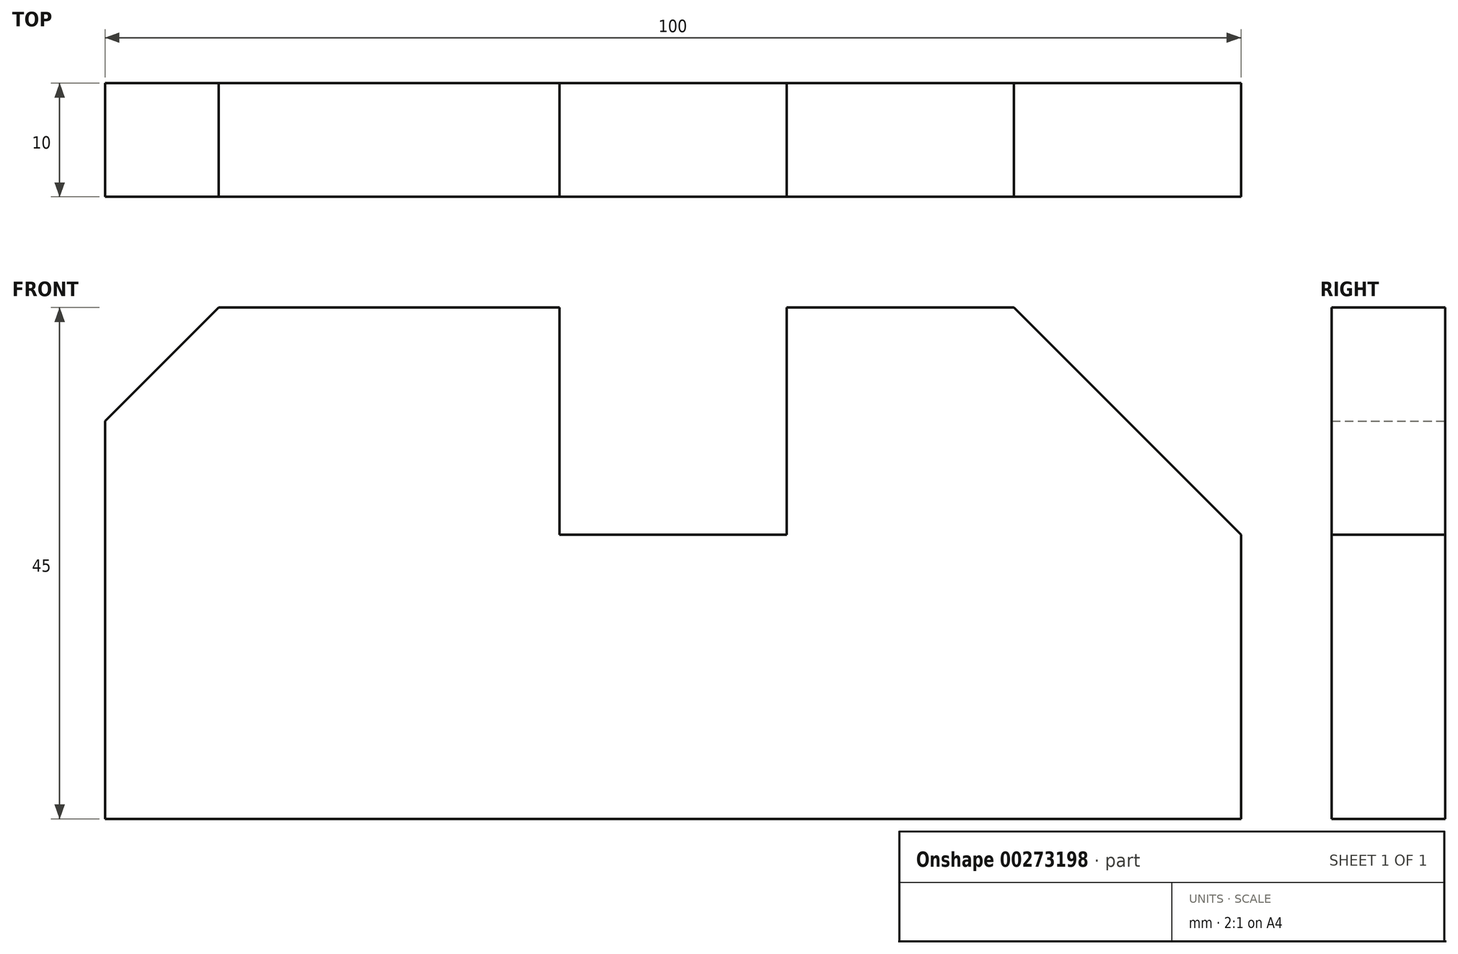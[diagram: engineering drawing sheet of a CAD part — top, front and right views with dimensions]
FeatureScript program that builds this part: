
annotation { "Feature Type Name" : "Feature", "Feature Type Description" : "" }
export const myFeature = defineFeature(function(context is Context, id is Id, definition is map)
    precondition{}
    {
        {
            var Q0;
            Q0=qCreatedBy(makeId("Front.planeOp"),FACE);
            var sketch = newSketch(context, id + "F0", { "sketchPlane" : qUnion([Q0])});
            skLineSegment(sketch, "E0", {"start": v(0, 0) * mm, "end": v(0, 35) * mm});
            skLineSegment(sketch, "E1", {"start": v(0, 35) * mm, "end": v(10, 45) * mm});
            skLineSegment(sketch, "E2", {"start": v(10, 45) * mm, "end": v(40, 45) * mm});
            skLineSegment(sketch, "E3", {"start": v(40, 45) * mm, "end": v(40, 25) * mm});
            skLineSegment(sketch, "E4", {"start": v(40, 25) * mm, "end": v(60, 25) * mm});
            skLineSegment(sketch, "E5", {"start": v(60, 25) * mm, "end": v(60, 45) * mm});
            skLineSegment(sketch, "E6", {"start": v(60, 45) * mm, "end": v(80, 45) * mm});
            skLineSegment(sketch, "E7", {"start": v(80, 45) * mm, "end": v(100, 25) * mm});
            skLineSegment(sketch, "E8", {"start": v(100, 25) * mm, "end": v(100, 0) * mm});
            skLineSegment(sketch, "E9", {"start": v(100, 0) * mm, "end": v(0, 0) * mm});
            skSolve(sketch);
        }
        {
            var Q0;
            Q0 = qSketchRegion(id + "F0", true);
            extrude(context, id + "F1", {"entities" : qUnion([Q0]), "depth" : 10 * mm});
        }
    });
